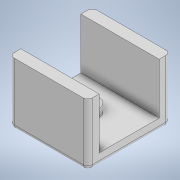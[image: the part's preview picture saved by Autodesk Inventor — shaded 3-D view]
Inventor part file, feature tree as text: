
AUTODESK INVENTOR PART (.ipt)
format: ipt  version: 2020 (Build 240168000, 168)  size: 202,240 bytes
history: native  units: in
note: dims shown in document units (in); Inventor stores cm internally (conversion verified against a paired STEP export)
features: extrude x8, sketch x8, chamfer x1, fillet x1
ambient origin geometry x8: Origin, YZ Plane, XZ Plane, XY Plane, X Axis, Y Axis, Z Axis, Center Point
bodies: Solid1 (feature_tree)
feature tree (18):
  extrude  "Extrusion1"  Depth=1.4331in
  extrude  "Extrusion2"  Depth=0.1969in
  extrude  "Extrusion3"  Depth=0.1969in
  extrude  "Extrusion4"  Depth=0.9606in TaperAngle=0.0deg
  extrude  "Extrusion5"  Depth=0.1969in
  chamfer  "Chamfer1"  Distance=0.1969in
  extrude  "Extrusion6"  Depth=0.1575in
  extrude  "Extrusion7"  Depth=0.2362in
  extrude  "Extrusion8"  Depth=0.1181in TaperAngle=0.0deg
  fillet  "Fillet2"  Radius=0.0787in
  sketch  "Sketch1"  dims[d0=2.3937in d1=1.4331in]
  sketch  "Sketch2"  dims[d2=0.1969in d3=0.0in d4=1.1811in]
  sketch  "Sketch3"  dims[d5=0.1969in d6=1.1811in]
  sketch  "Sketch4"  dims[d7=0.1969in d8=0.9606in d9=0.0in]
  sketch  "Sketch5"  dims[d10=0.3406in d11=0.3406in d12=0.1969in d13=0.0in]
  sketch  "Sketch6"  dims[d14=0.1575in d15=0.1575in]
  sketch  "Sketch7"  dims[d16=0.5906in d17=0.0in d18=0.2362in]
  sketch  "Sketch8"  dims[d19=0.2362in d20=0.1181in d21=0.0in d22=0.0591in d23=0.0787in d24=45.0deg d26=1.3543in d27=1.9685in d28=0.0in d29=0.1969in d30=0.1969in d31=1.063in d32=0.0in d33=0.0787in d34=0.0in d35=0.0787in]
